# Revit family: Haworth_Epure_SquareDesk_EU_PRELIMINARY
name_source: partatom
category: Furniture
units: mm (PartAtom-declared; Revit-internal decimal feet)

## family parameters
Always vertical = Yes
Cut with Voids When Loaded = No
OmniClass Number = 23.40.70.14.64.11
OmniClass Title = Office Furniture
Room Calculation Point = No
Shared = No
Work Plane-Based = No

## types (2) — shared parameters
Actual Height = 73 cm
Assembly Code = E2020200
Description = Haworth - Epure - Square Desk
Flip Top Finish = Haworth _ Paint _ Metallic Silver
Leg Height = 70 cm
Manufacturer = Haworth
Model = EUSD1X1X
Revision Number = 1
Size = Verify Final Dim.w/ Haworth
Trim Finish = Haworth _ Metal _ Structured White EC
URL = https://www.haworth.com
URL - Product = https://www.haworth.com
Warranty = http://www.haworth.com

## per-type parameters (varying)
| type | Actual Depth | Actual Width | Flip Top Cable Outlet | Rounded Corners | Squared Corners |
| 140 x 140 | 140 cm | 140 cm | No | Yes | No |
| 160 x 160 | 160 cm | 160 cm | Yes | No | Yes |

## geometry (parser evidence)
native form markers: Blend x4, Sweep x12
no freeform markers — native parametric forms only
